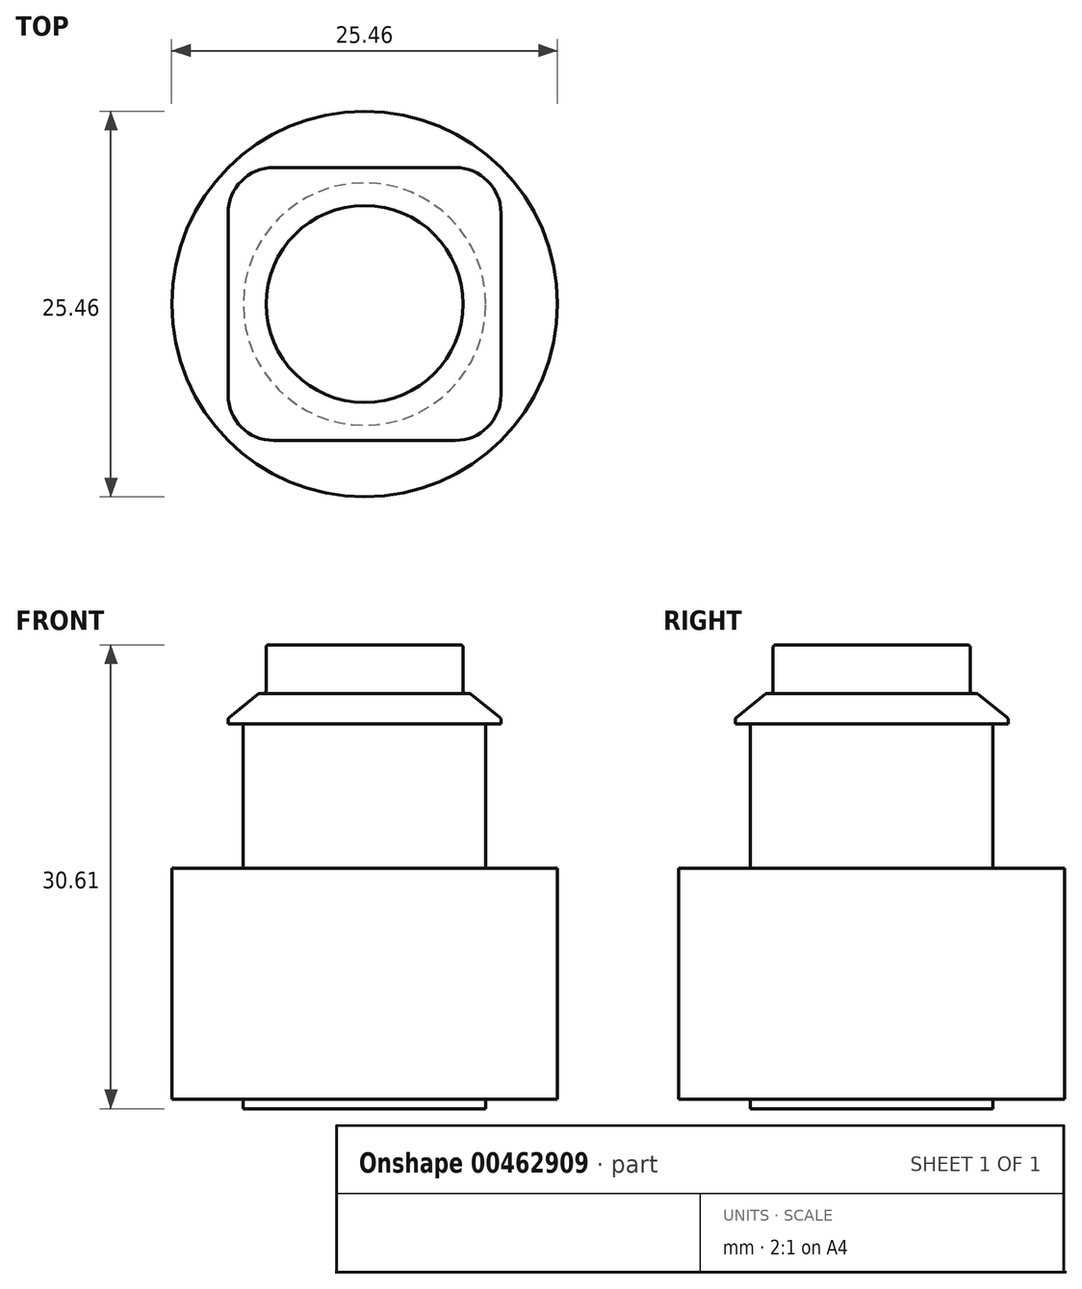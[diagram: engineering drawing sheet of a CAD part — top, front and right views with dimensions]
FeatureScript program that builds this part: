
annotation { "Feature Type Name" : "Feature", "Feature Type Description" : "" }
export const myFeature = defineFeature(function(context is Context, id is Id, definition is map)
    precondition{}
    {
        {
            var Q0;
            Q0=qCreatedBy(makeId("Top.planeOp"),FACE);
            var sketch = newSketch(context, id + "F0", { "sketchPlane" : qUnion([Q0])});
            skLineSegment(sketch, "E0.bottom", {"start": v(6, 9) * mm, "end": v(-6, 9) * mm});
            skLineSegment(sketch, "E0.top", {"start": v(6, -9) * mm, "end": v(-6, -9) * mm});
            skLineSegment(sketch, "E0.left", {"start": v(9, 6) * mm, "end": v(9, -6) * mm});
            skLineSegment(sketch, "E0.right", {"start": v(-9, 6) * mm, "end": v(-9, -6) * mm});
            skPoint(sketch, "E0.middle", {"position": v(0, 0) * mm});
            skPoint(sketch, "E1.visualSharp", {"position": v(-9, 9) * mm});
            skArc(sketch, "E1.filletArc", {"start": v(-6, 9) * mm, "mid": v(-8.12, 8.12) * mm, "end": v(-9, 6) * mm});
            skPoint(sketch, "E2.visualSharp", {"position": v(9, 9) * mm});
            skArc(sketch, "E2.filletArc", {"start": v(9, 6) * mm, "mid": v(8.12, 8.12) * mm, "end": v(6, 9) * mm});
            skPoint(sketch, "E3.visualSharp", {"position": v(9, -9) * mm});
            skArc(sketch, "E3.filletArc", {"start": v(6, -9) * mm, "mid": v(8.12, -8.12) * mm, "end": v(9, -6) * mm});
            skPoint(sketch, "E4.visualSharp", {"position": v(-9, -9) * mm});
            skArc(sketch, "E4.filletArc", {"start": v(-9, -6) * mm, "mid": v(-8.12, -8.12) * mm, "end": v(-6, -9) * mm});
            skCircle(sketch, "E5", {"center": v(0, 0) * mm, "radius": 6.5 * mm});
            skCircle(sketch, "E6", {"center": v(0, 0) * mm, "radius": 8 * mm});
            skLineSegment(sketch, "E7", {"start": v(-2.78, 7.5) * mm, "end": v(2.78, 7.5) * mm});
            skLineSegment(sketch, "E8", {"start": v(-2.78, -7.5) * mm, "end": v(2.78, -7.5) * mm});
            skLineSegment(sketch, "E9", {"start": v(0, 0) * mm, "end": v(0, 7.5) * mm, "construction": true});
            skPoint(sketch, "E10", {"position": v(0, 7.5) * mm});
            skCircle(sketch, "E11", {"center": v(0, 0) * mm, "radius": 6.17 * mm});
            skSolve(sketch);
        }
        {
            var Q0;
            {var subQ0=sQuery(id+"F0.wireOp",EDGE,"E7");Q0=makeQuery(id+"F0.imprint","IMPRINT",FACE,{"disambiguationData":[TD([[makeQuery(id+"F0.imprint","IMPRINT",EDGE,{"derivedFrom":subQ0}),1.0]])]});}
            var Q1;
            {var subQ0=sQuery(id+"F0.wireOp",EDGE,"E8");Q1=makeQuery(id+"F0.imprint","IMPRINT",FACE,{"disambiguationData":[TD([[makeQuery(id+"F0.imprint","IMPRINT",EDGE,{"derivedFrom":subQ0}),-1.0]])]});}
            var Q2;
            Q2=makeQuery(id+"F0.imprint","IMPRINT",FACE,{"disambiguationData":[TD([[makeQuery(id+"F0.imprint","IMPRINT",EDGE,{"derivedFrom":sQuery(id+"F0.wireOp",EDGE,"E5")}),-1.0]])]});
            var Q3;
            Q3=makeQuery(id+"F0.imprint","IMPRINT",FACE,{"disambiguationData":[TD([[makeQuery(id+"F0.imprint","IMPRINT",EDGE,{"derivedFrom":sQuery(id+"F0.wireOp",EDGE,"E0.bottom")}),1.0]])]});
            extrude(context, id + "F1", {"entities" : qUnion([Q0, Q1, Q2, Q3]), "depth" : 2 * mm, "offsetDistance" : 25.4 * mm});
        }
        {
            var Q0;
            Q0=makeQuery(id+"F0.imprint","IMPRINT",FACE,{"disambiguationData":[TD([[makeQuery(id+"F0.imprint","IMPRINT",EDGE,{"derivedFrom":sQuery(id+"F0.wireOp",EDGE,"E5")}),1.0]])]});
            var Q1;
            Q1=makeQuery(id+"F0.imprint","IMPRINT",FACE,{"disambiguationData":[TD([[makeQuery(id+"F0.imprint","IMPRINT",EDGE,{"derivedFrom":sQuery(id+"F0.wireOp",EDGE,"E11")}),1.0]])]});
            extrude(context, id + "F2", {"entities" : qUnion([Q0, Q1]), "depth" : 5.2 * mm, "offsetDistance" : 25.4 * mm});
        }
        {
            var Q0;
            Q0=makeQuery(id+"F0.imprint","IMPRINT",FACE,{"disambiguationData":[TD([[makeQuery(id+"F0.imprint","IMPRINT",EDGE,{"derivedFrom":sQuery(id+"F0.wireOp",EDGE,"E11")}),1.0]])]});
            extrude(context, id + "F3", {"entities" : qUnion([Q0]), "depth" : 4.8 * mm, "offsetDistance" : 25.4 * mm});
        }
        {
            var Q0;
            Q0=makeQuery(id+"F0.imprint","IMPRINT",FACE,{"disambiguationData":[TD([[makeQuery(id+"F0.imprint","IMPRINT",EDGE,{"derivedFrom":sQuery(id+"F0.wireOp",EDGE,"E5")}),1.0]])]});
            var Q1;
            Q1=makeQuery(id+"F0.imprint","IMPRINT",FACE,{"disambiguationData":[TD([[makeQuery(id+"F0.imprint","IMPRINT",EDGE,{"derivedFrom":sQuery(id+"F0.wireOp",EDGE,"E5")}),-1.0]])]});
            var Q2;
            Q2=makeQuery(id+"F0.imprint","IMPRINT",FACE,{"disambiguationData":[TD([[makeQuery(id+"F0.imprint","IMPRINT",EDGE,{"derivedFrom":sQuery(id+"F0.wireOp",EDGE,"E11")}),1.0]])]});
            extrude(context, id + "F4", {"entities" : qUnion([Q0, Q1, Q2]), "operationType" : NewBodyOperationType.ADD, "oppositeDirection" : true, "depth" : 24 * mm - 5.5 * mm, "offsetDistance" : 25.4 * mm});
        }
        {
            var Q0;
            Q0=makeQuery(id+"F0.imprint","IMPRINT",FACE,{"disambiguationData":[TD([[makeQuery(id+"F0.imprint","IMPRINT",EDGE,{"derivedFrom":sQuery(id+"F0.wireOp",EDGE,"E0.bottom")}),1.0]])]});
            cPlane(context, id + "F5", {"entities" : qUnion([Q0]), "cplaneType" : CPlaneType.OFFSET, "offset" : 24 * mm, "oppositeDirection" : true, "width" : 152.4 * mm, "height" : 152.4 * mm});
        }
        {
            var Q0;
            Q0=qCreatedBy(id+"F5.planeOp",FACE);
            var sketch = newSketch(context, id + "F6", { "sketchPlane" : qUnion([Q0])});
            skLineSegment(sketch, "E12.bottom", {"start": v(-4, -1) * mm, "end": v(-3, -1) * mm});
            skLineSegment(sketch, "E12.top", {"start": v(-4, 1) * mm, "end": v(-3, 1) * mm});
            skLineSegment(sketch, "E12.left", {"start": v(-4, -1) * mm, "end": v(-4, 1) * mm});
            skLineSegment(sketch, "E12.right", {"start": v(-3, -1) * mm, "end": v(-3, 1) * mm});
            skLineSegment(sketch, "E13.bottom", {"start": v(-4.68, 2.29) * mm, "end": v(-3.68, 2.29) * mm});
            skLineSegment(sketch, "E13.top", {"start": v(-4.68, 4.29) * mm, "end": v(-3.68, 4.29) * mm});
            skLineSegment(sketch, "E13.left", {"start": v(-4.68, 2.29) * mm, "end": v(-4.68, 4.29) * mm});
            skLineSegment(sketch, "E13.right", {"start": v(-3.68, 2.29) * mm, "end": v(-3.68, 4.29) * mm});
            skPoint(sketch, "E14", {"position": v(-3, 0) * mm});
            skLineSegment(sketch, "E15", {"start": v(0, 0) * mm, "end": v(-3, 0) * mm, "construction": true});
            skSolve(sketch);
        }
        {
            var Q0;
            Q0=makeQuery(id+"F6.imprint","IMPRINT",FACE,{"disambiguationData":[TD([[makeQuery(id+"F6.imprint","IMPRINT",EDGE,{"derivedFrom":sQuery(id+"F6.wireOp",EDGE,"E12.bottom")}),1.0]])]});
            var Q1;
            Q1=makeQuery(id+"F6.imprint","IMPRINT",FACE,{"disambiguationData":[TD([[makeQuery(id+"F6.imprint","IMPRINT",EDGE,{"derivedFrom":sQuery(id+"F6.wireOp",EDGE,"E13.bottom")}),1.0]])]});
            extrude(context, id + "F7", {"entities" : qUnion([Q0, Q1]), "operationType" : NewBodyOperationType.ADD, "endBound" : BoundingType.UP_TO_NEXT, "depth" : 25.4 * mm, "offsetDistance" : 25.4 * mm});
        }
        {
            var Q0;
            {var subQ0=sQuery(id+"F0.wireOp",EDGE,"E8");Q0=makeQuery(id+"F0.imprint","IMPRINT",FACE,{"disambiguationData":[TD([[makeQuery(id+"F0.imprint","IMPRINT",EDGE,{"derivedFrom":subQ0}),-1.0]])]});}
            var Q1;
            {var subQ0=sQuery(id+"F0.wireOp",EDGE,"E7");Q1=makeQuery(id+"F0.imprint","IMPRINT",FACE,{"disambiguationData":[TD([[makeQuery(id+"F0.imprint","IMPRINT",EDGE,{"derivedFrom":subQ0}),1.0]])]});}
            var Q2;
            Q2=makeQuery(id+"F0.imprint","IMPRINT",FACE,{"disambiguationData":[TD([[makeQuery(id+"F0.imprint","IMPRINT",EDGE,{"derivedFrom":sQuery(id+"F0.wireOp",EDGE,"E5")}),1.0]])]});
            var Q3;
            Q3=makeQuery(id+"F0.imprint","IMPRINT",FACE,{"disambiguationData":[TD([[makeQuery(id+"F0.imprint","IMPRINT",EDGE,{"derivedFrom":sQuery(id+"F0.wireOp",EDGE,"E5")}),-1.0]])]});
            var Q4;
            Q4=makeQuery(id+"F0.imprint","IMPRINT",FACE,{"disambiguationData":[TD([[makeQuery(id+"F0.imprint","IMPRINT",EDGE,{"derivedFrom":sQuery(id+"F0.wireOp",EDGE,"E11")}),1.0]])]});
            extrude(context, id + "F8", {"entities" : qUnion([Q0, Q1, Q2, Q3, Q4]), "oppositeDirection" : true, "depth" : 25.4 * mm, "offsetDistance" : 25.4 * mm, "hasSecondDirection" : true, "secondDirectionOppositeDirection" : false, "secondDirectionDepth" : 0.25 * mm});
        }
        {
            var Q0;
            Q0=makeQuery(id+"F0.imprint","IMPRINT",FACE,{"disambiguationData":[TD([[makeQuery(id+"F0.imprint","IMPRINT",EDGE,{"derivedFrom":sQuery(id+"F0.wireOp",EDGE,"E0.bottom")}),1.0]])]});
            cPlane(context, id + "F9", {"entities" : qUnion([Q0]), "cplaneType" : CPlaneType.OFFSET, "offset" : 9.52 * mm, "oppositeDirection" : true, "width" : 152.4 * mm, "height" : 152.4 * mm});
        }
        {
            var Q0;
            Q0=qCreatedBy(id+"F9.planeOp",FACE);
            var sketch = newSketch(context, id + "F10", { "sketchPlane" : qUnion([Q0])});
            skCircle(sketch, "E16", {"center": v(0, 0) * mm, "radius": 12.73 * mm});
            skSolve(sketch);
        }
        {
            var Q0;
            Q0 = qSketchRegion(id + "F10", true);
            extrude(context, id + "F11", {"entities" : qUnion([Q0]), "operationType" : NewBodyOperationType.ADD, "oppositeDirection" : true, "depth" : 15.24 * mm, "offsetDistance" : 25.4 * mm});
        }
        {
            var Q0;
            Q0=makeQuery(id+"F1.opExtrude","CAP_EDGE",EDGE,{"disambiguationData":[OSD([sQuery(id+"F0.wireOp",EDGE,"E3.filletArc")])],"isStart":false});
            chamfer(context, id + "F12", {"entities" : qUnion([Q0]), "chamferType" : ChamferType.TWO_OFFSETS, "width1" : 2.03 * mm, "oppositeDirection" : false, "width2" : 1.65 * mm, "tangentPropagation" : true});
        }
        {
            var Q0;
            Q0=makeQuery(id+"F2.opExtrude","CAP_FACE",FACE,{"disambiguationData":[OSD([sQuery(id+"F0.wireOp",EDGE,"E5")])],"isStart":false});
            var Q1;
            Q1=makeQuery(id+"F1.opExtrude","CAP_EDGE",EDGE,{"disambiguationData":[OSD([sQuery(id+"F0.wireOp",EDGE,"E5")])],"isStart":false});
            var Q2;
            Q2=makeQuery(id+"F1.opExtrude","CAP_FACE",FACE,{"disambiguationData":[OSD([sQuery(id+"F0.wireOp",EDGE,"E0.bottom"),sQuery(id+"F0.wireOp",EDGE,"E0.top"),sQuery(id+"F0.wireOp",EDGE,"E0.left"),sQuery(id+"F0.wireOp",EDGE,"E0.right"),sQuery(id+"F0.wireOp",EDGE,"E1.filletArc"),sQuery(id+"F0.wireOp",EDGE,"E2.filletArc"),sQuery(id+"F0.wireOp",EDGE,"E3.filletArc"),sQuery(id+"F0.wireOp",EDGE,"E4.filletArc"),sQuery(id+"F0.wireOp",EDGE,"E5")])],"isStart":false});
            var Q3;
            {var subQ0=sQuery(id+"F0.wireOp",EDGE,"E2.filletArc");Q3=makeQuery(id+"F12.opChamfer","BLEND_EDGE",EDGE,{"blendedFrom":[makeQuery(id+"F1.opExtrude","CAP_EDGE",EDGE,{"disambiguationData":[OSD([subQ0])],"isStart":false}),makeQuery(id+"F1.opExtrude","SWEPT_FACE",FACE,{"disambiguationData":[OSD([subQ0])]})],"blendedInto":[makeQuery(id+"F1.opExtrude","SWEPT_FACE",FACE,{"disambiguationData":[OSD([subQ0])]})]});}
            fillet(context, id + "F13", {"entities" : qUnion([Q0, Q1, Q2, Q3]), "radius" : 0.18 * mm, "tangentPropagation" : true, "allowEdgeOverflow" : false});
        }
    });
